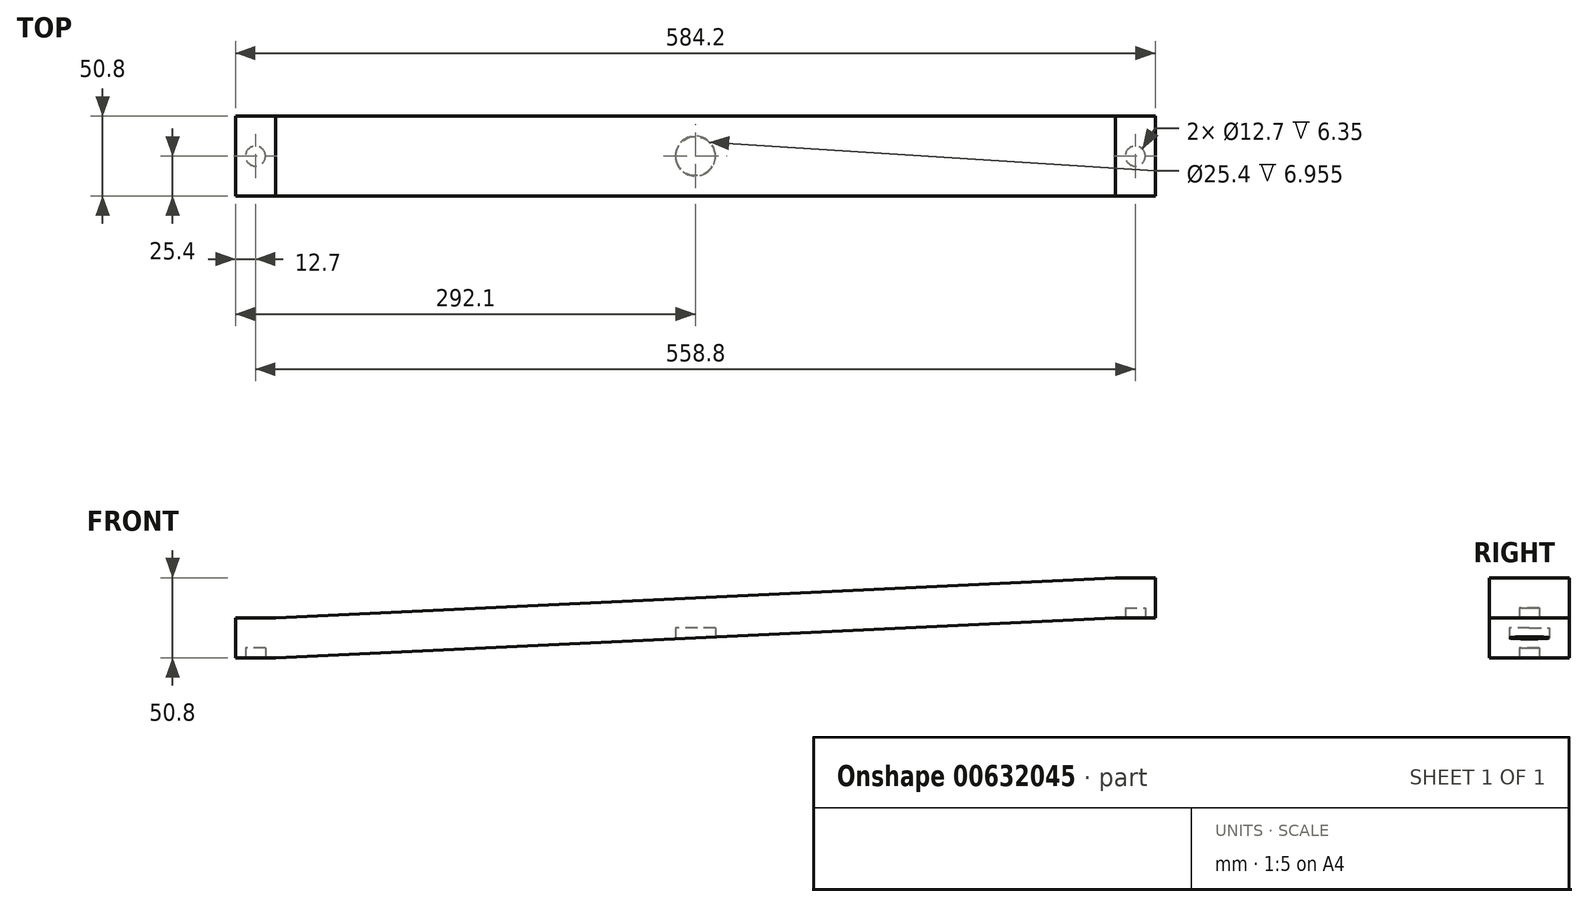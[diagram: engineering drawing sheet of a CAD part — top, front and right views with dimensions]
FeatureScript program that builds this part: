
annotation { "Feature Type Name" : "Feature", "Feature Type Description" : "" }
export const myFeature = defineFeature(function(context is Context, id is Id, definition is map)
    precondition{}
    {
        {
            var Q0;
            Q0=qCreatedBy(makeId("Front.planeOp"),FACE);
            var sketch = newSketch(context, id + "F0", { "sketchPlane" : qUnion([Q0])});
            skLineSegment(sketch, "E0", {"start": v(0, 0) * mm, "end": v(0, 25.4) * mm});
            skLineSegment(sketch, "E1", {"start": v(0, 25.4) * mm, "end": v(25.4, 25.4) * mm});
            skLineSegment(sketch, "E2", {"start": v(25.4, 25.4) * mm, "end": v(558.8, 50.8) * mm});
            skLineSegment(sketch, "E3", {"start": v(558.8, 50.8) * mm, "end": v(584.2, 50.8) * mm});
            skLineSegment(sketch, "E4", {"start": v(584.2, 50.8) * mm, "end": v(584.2, 25.4) * mm});
            skLineSegment(sketch, "E5", {"start": v(584.2, 25.4) * mm, "end": v(558.8, 25.4) * mm});
            skLineSegment(sketch, "E6", {"start": v(558.8, 25.4) * mm, "end": v(25.4, 0) * mm});
            skLineSegment(sketch, "E7", {"start": v(25.4, 0) * mm, "end": v(0, 0) * mm});
            skSolve(sketch);
        }
        {
            var Q0;
            Q0 = qSketchRegion(id + "F0", true);
            extrude(context, id + "F1", {"entities" : qUnion([Q0]), "depth" : 50.8 * mm, "offsetDistance" : 25.4 * mm});
        }
        {
            var Q0;
            Q0=qCreatedBy(makeId("Top.planeOp"),FACE);
            var sketch = newSketch(context, id + "F2", { "sketchPlane" : qUnion([Q0])});
            skCircle(sketch, "E8", {"center": v(12.7, -25.4) * mm, "radius": 6.35 * mm});
            skCircle(sketch, "E9", {"center": v(571.5, -25.4) * mm, "radius": 6.35 * mm});
            skCircle(sketch, "E10", {"center": v(292.1, -25.4) * mm, "radius": 12.7 * mm});
            skSolve(sketch);
        }
        {
            var Q0;
            Q0=makeQuery(id+"F2.imprint","IMPRINT",FACE,{"disambiguationData":[TD([[makeQuery(id+"F2.imprint","IMPRINT",EDGE,{"derivedFrom":sQuery(id+"F2.wireOp",EDGE,"E8")}),1.0]])]});
            extrude(context, id + "F3", {"entities" : qUnion([Q0]), "operationType" : NewBodyOperationType.REMOVE, "depth" : 6.35 * mm, "offsetDistance" : 25.4 * mm});
        }
        {
            var Q0;
            Q0=qCreatedBy(makeId("Top.planeOp"),FACE);
            var sketch = newSketch(context, id + "F4", { "sketchPlane" : qUnion([Q0])});
            skCircle(sketch, "E11", {"center": v(292.1, -25.4) * mm, "radius": 12.7 * mm});
            skSolve(sketch);
        }
        {
            var Q0;
            Q0 = qSketchRegion(id + "F4", true);
            extrude(context, id + "F5", {"entities" : qUnion([Q0]), "operationType" : NewBodyOperationType.REMOVE, "depth" : 19.05 * mm, "offsetDistance" : 25.4 * mm});
        }
        {
            var Q0;
            Q0=makeQuery(id+"F1.opExtrude","SWEPT_FACE",FACE,{"disambiguationData":[OSD([sQuery(id+"F0.wireOp",EDGE,"E5")])]});
            var sketch = newSketch(context, id + "F6", { "sketchPlane" : qUnion([Q0])});
            skCircle(sketch, "E12", {"center": v(571.5, 25.4) * mm, "radius": 6.35 * mm});
            skPoint(sketch, "E12.centerSnap0", {"position": v(584.2, 25.4) * mm});
            skPoint(sketch, "E12.centerSnap1", {"position": v(571.5, 0) * mm});
            skSolve(sketch);
        }
        {
            var Q0;
            Q0 = qSketchRegion(id + "F6", true);
            extrude(context, id + "F7", {"entities" : qUnion([Q0]), "operationType" : NewBodyOperationType.REMOVE, "oppositeDirection" : true, "depth" : 6.35 * mm, "offsetDistance" : 25.4 * mm});
        }
    });
